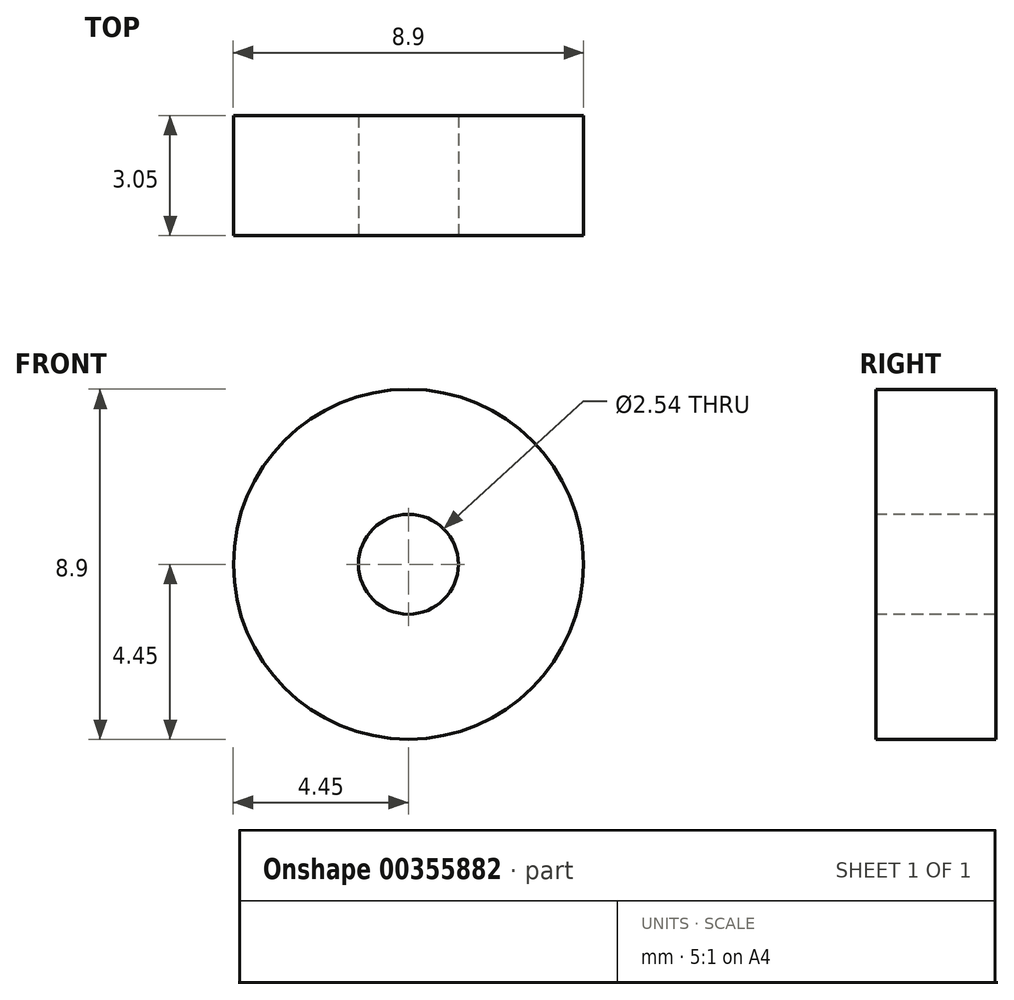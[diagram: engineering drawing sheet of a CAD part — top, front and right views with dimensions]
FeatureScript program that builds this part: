
annotation { "Feature Type Name" : "Feature", "Feature Type Description" : "" }
export const myFeature = defineFeature(function(context is Context, id is Id, definition is map)
    precondition{}
    {
        {
            var Q0;
            Q0=qCreatedBy(makeId("Front.planeOp"),FACE);
            var sketch = newSketch(context, id + "F0", { "sketchPlane" : qUnion([Q0])});
            skCircle(sketch, "E0", {"center": v(0, 0) * mm, "radius": 4.45 * mm});
            skSolve(sketch);
        }
        {
            var Q0;
            Q0=makeQuery(id+"F0.imprint","IMPRINT",FACE,{"disambiguationData":[TD([[makeQuery(id+"F0.imprint","IMPRINT",EDGE,{"derivedFrom":sQuery(id+"F0.wireOp",EDGE,"E0")}),1.0]])]});
            extrude(context, id + "F1", {"entities" : qUnion([Q0]), "depth" : 3.05 * mm});
        }
        {
            var Q0;
            Q0=makeQuery(id+"F1.opExtrude","CAP_FACE",FACE,{"disambiguationData":[OSD([sQuery(id+"F0.wireOp",EDGE,"E0")])],"isStart":false});
            var sketch = newSketch(context, id + "F2", { "sketchPlane" : qUnion([Q0])});
            skCircle(sketch, "E1", {"center": v(0, 0) * mm, "radius": 1.27 * mm});
            skSolve(sketch);
        }
        {
            var Q0;
            Q0=qSketchRegion(id+"F2",true);
            extrude(context, id + "F3", {"entities" : qUnion([Q0]), "operationType" : NewBodyOperationType.REMOVE, "oppositeDirection" : true, "depth" : 25.4 * mm});
        }
    });
